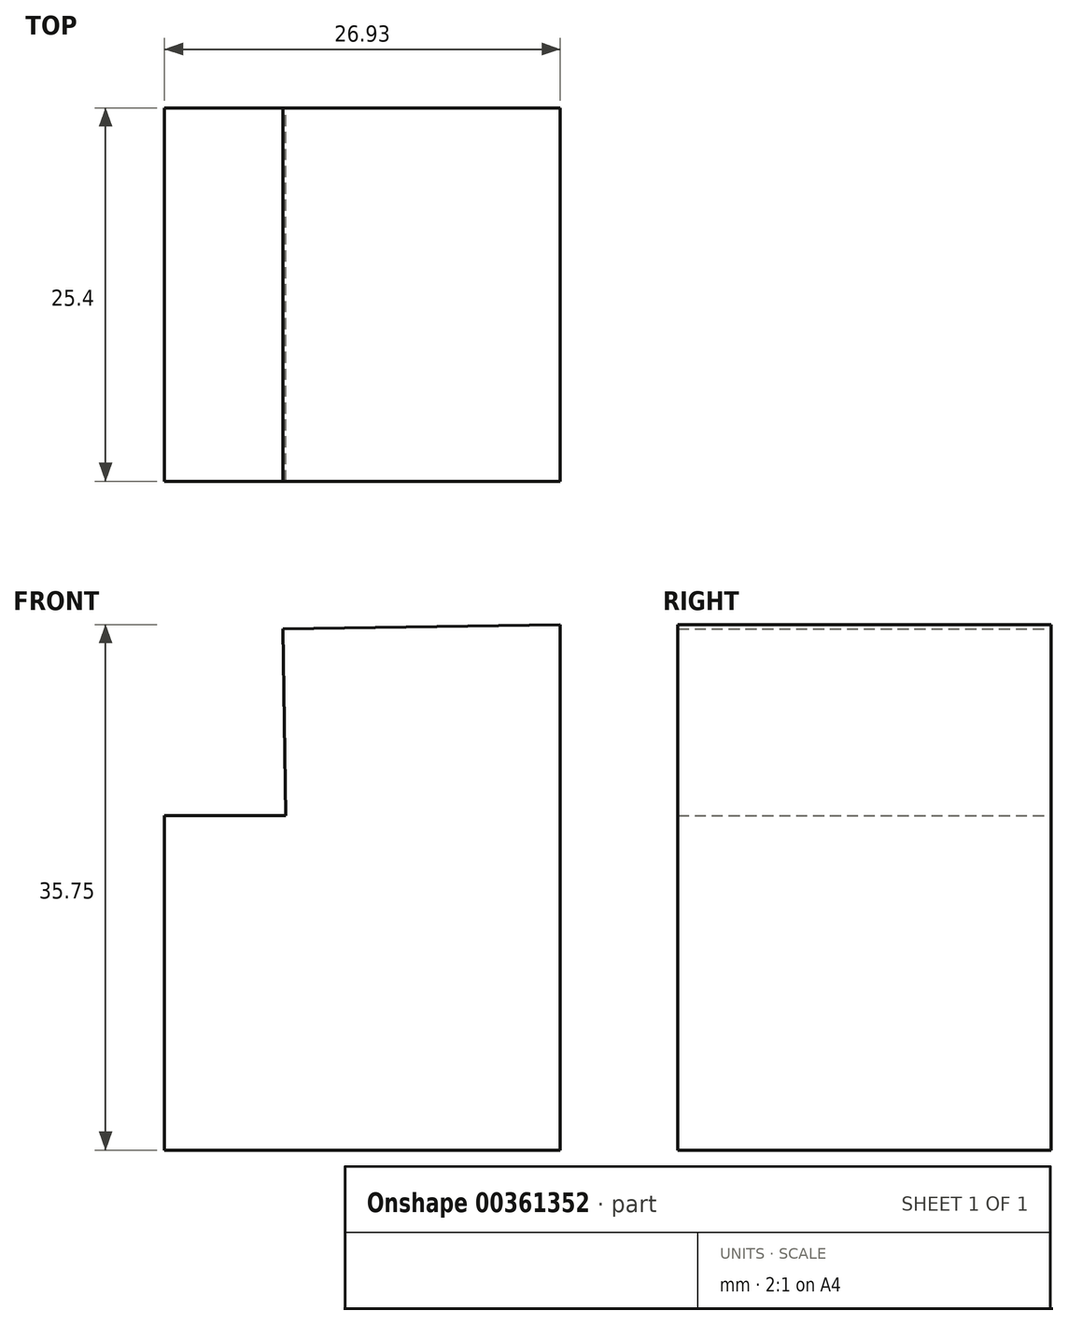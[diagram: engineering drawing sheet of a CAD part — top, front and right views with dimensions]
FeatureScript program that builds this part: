
annotation { "Feature Type Name" : "Feature", "Feature Type Description" : "" }
export const myFeature = defineFeature(function(context is Context, id is Id, definition is map)
    precondition{}
    {
        {
            var Q0;
            Q0=qCreatedBy(makeId("Front.planeOp"),FACE);
            var sketch = newSketch(context, id + "F0", { "sketchPlane" : qUnion([Q0])});
            skLineSegment(sketch, "E0", {"start": v(-49.83, 35.44) * mm, "end": v(-49.83, 0) * mm});
            skLineSegment(sketch, "E1", {"start": v(-49.83, 0) * mm, "end": v(-29.1, 0) * mm});
            skLineSegment(sketch, "E2", {"start": v(-29.1, 0) * mm, "end": v(-29.1, 22.75) * mm});
            skLineSegment(sketch, "E3", {"start": v(-29.1, 22.75) * mm, "end": v(-13.62, 22.75) * mm});
            skLineSegment(sketch, "E4", {"start": v(-13.62, 22.75) * mm, "end": v(-13.62, 0) * mm});
            skLineSegment(sketch, "E5", {"start": v(-13.62, 0) * mm, "end": v(13.3, 0) * mm});
            skLineSegment(sketch, "E6", {"start": v(13.3, 0) * mm, "end": v(13.3, 35.75) * mm});
            skLineSegment(sketch, "E7", {"start": v(13.3, 35.75) * mm, "end": v(-5.57, 35.44) * mm});
            skLineSegment(sketch, "E8", {"start": v(-5.57, 35.44) * mm, "end": v(-5.36, 22.75) * mm});
            skLineSegment(sketch, "E9", {"start": v(-5.36, 22.75) * mm, "end": v(-13.62, 22.75) * mm});
            skLineSegment(sketch, "E10", {"start": v(-32.19, 35.44) * mm, "end": v(-49.83, 35.44) * mm});
            skLineSegment(sketch, "E11", {"start": v(-32.19, 28.01) * mm, "end": v(-32.19, 35.44) * mm});
            skLineSegment(sketch, "E12", {"start": v(-29.1, 22.75) * mm, "end": v(-32.19, 22.75) * mm});
            skLineSegment(sketch, "E13", {"start": v(-32.19, 22.75) * mm, "end": v(-32.19, 28.01) * mm});
            skSolve(sketch);
        }
        {
            var Q0;
            Q0=makeQuery(id+"F0.imprint","IMPRINT",FACE,{"disambiguationData":[TD([[makeQuery(id+"F0.imprint","IMPRINT",EDGE,{"derivedFrom":sQuery(id+"F0.wireOp",EDGE,"E4")}),1.0]])]});
            extrude(context, id + "F1", {"entities" : qUnion([Q0]), "depth" : 25.4 * mm});
        }
    });
